# Revit family: IS_Tempo_Multiproduct_BIM_GB_T6792;T6793
name_source: partatom
category: Plumbing Fixtures
revit_build: Autodesk Revit MEP 2012 (Build: 20110309_2315(x64)
units: mm (PartAtom-declared; Revit-internal decimal feet)

## types (2) — shared parameters
Accessories = www.idealspec.co.uk
Assembly Code = C1030200
AssetType = Fixed
BIMObjectName = TOILETSEAT_IdealStandard_Tempo-AllVariants
BREEAM Approved = No
Brand = Ideal Standard International Ltd
Category = SanitaryTerminal_TOILETPAN_UK
Color = White
ConnectionType = Plumbing
CurrentRevision = 1
Default Elevation = 1219 mm
DurationUnit = Years
ECA = No
ElementType = TOILETPAN: Soil appliance for the disposal of excrement
ExpectedLife = 15
Finish = White
Help = http://www.idealspec.co.uk
InstallationDate = 0
InstallationInstructions = http://www.idealspec.co.uk
Manufacturer = Ideal Standard International Ltd
ManufacturerURL = www.idealspec.co.uk
Material = Plastic
NBSReference = 300
Name = TOILETSEAT_IdealStandard_Tempo-AllVariants
NettWeight = 2.3Kg
NominalHeight = 40 mm  [stored 0.131234 ft]
NominalLength = 425 mm
NominalWidth = 358 mm
PredefinedType = toiletpan
ProductDataSheet = http://www.idealspec.co.uk
ProductInformation = http://www.idealspec.co.uk
SalesInformation = http://www.idealspec.co.uk
SendEnquiry = http://www.idealspec.co.uk
Shape = Soft Square
Size = 425mm x 358mm x 40mm
Space = Internal
SpareParts = www.fastpart-spares.co.uk
URL = www.idealspec.co.uk
Version = 1
VolumeUnits = Litres
WRAS = No
WarrantyDescription = Manufacturers Warranty
WarrantyDurationParts = 5
WarrantyDurationUnit = Years
WarrantyGuarantorParts = Ideal Standard International Ltd
WarrantyStartDate = 0
WaterEfficientProduct = No

## per-type parameters (varying)
| type | Description | Features | Model | ModelNumber | ModelReference | PartNumber |
| T679201 - Tempo Seat & Cover | Tempo Seat & Cover | Standard Close | T697201 | T697201 | T697201 | T697201 |
| T697301 - Tempo Seat & Cover, Slow Close | Tempo Seat & Cover,  Slow Close | Slow Close | T697301 | T697301 | T697301 | T697301 |

note: [stored X ft] marks values corroborated as IEEE doubles in the binary element streams (Revit-internal decimal feet)

## geometry (parser evidence)
native form markers: Blend x2, Sweep x4
no freeform markers — native parametric forms only
